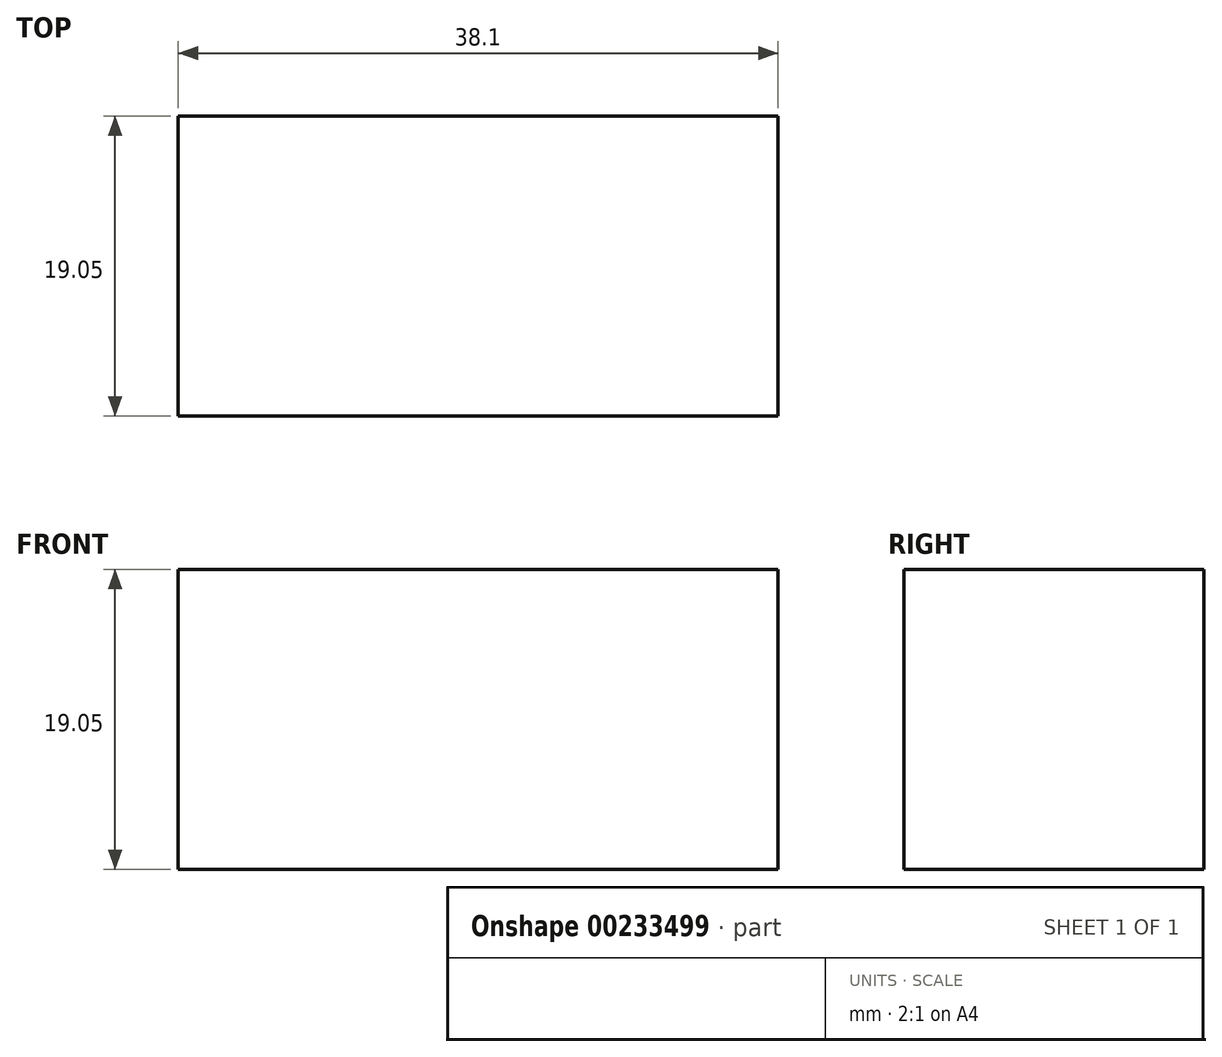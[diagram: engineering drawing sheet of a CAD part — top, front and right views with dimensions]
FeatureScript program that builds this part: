
annotation { "Feature Type Name" : "Feature", "Feature Type Description" : "" }
export const myFeature = defineFeature(function(context is Context, id is Id, definition is map)
    precondition{}
    {
        {
            var Q0;
            Q0=qCreatedBy(makeId("Front.planeOp"),FACE);
            var sketch = newSketch(context, id + "F0", { "sketchPlane" : qUnion([Q0])});
            skLineSegment(sketch, "E0.bottom", {"start": v(23.2, -11.77) * mm, "end": v(61.3, -11.77) * mm});
            skLineSegment(sketch, "E0.top", {"start": v(23.2, -30.82) * mm, "end": v(61.3, -30.82) * mm});
            skLineSegment(sketch, "E0.left", {"start": v(23.2, -11.77) * mm, "end": v(23.2, -30.82) * mm});
            skLineSegment(sketch, "E0.right", {"start": v(61.3, -11.77) * mm, "end": v(61.3, -30.82) * mm});
            skSolve(sketch);
        }
        {
            var Q0;
            Q0 = qSketchRegion(id + "F0", true);
            extrude(context, id + "F1", {"entities" : qUnion([Q0]), "depth" : 19.05 * mm});
        }
    });
